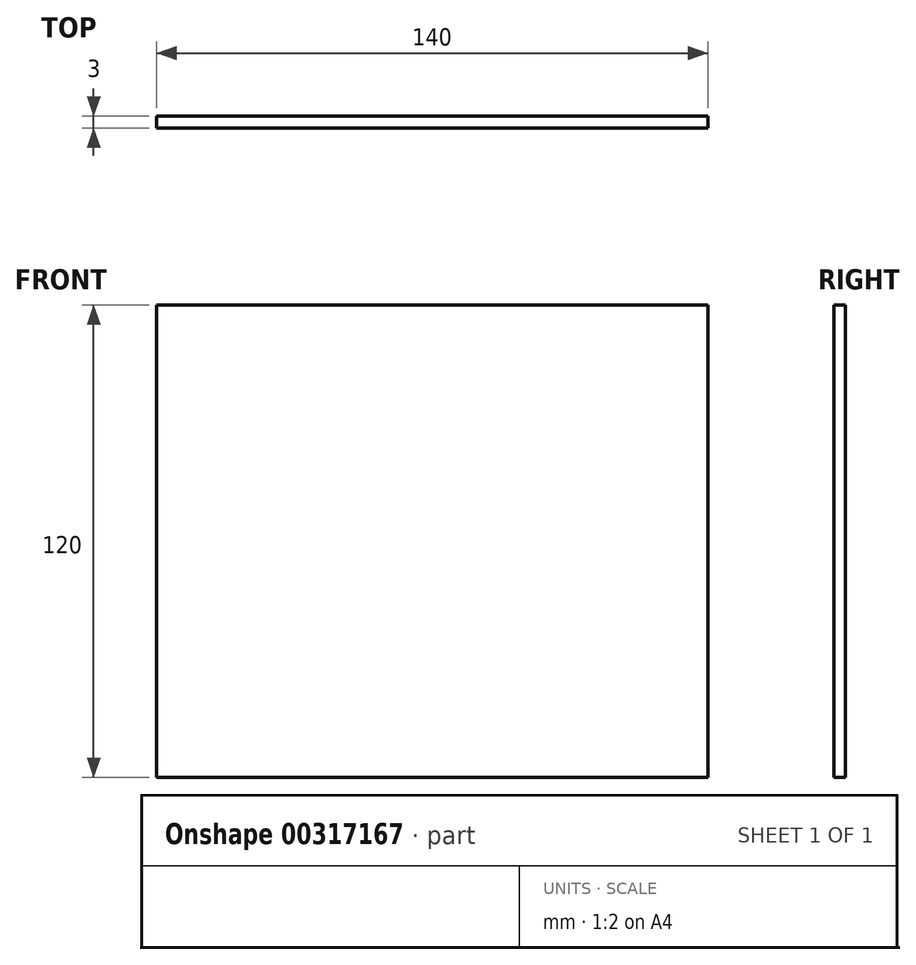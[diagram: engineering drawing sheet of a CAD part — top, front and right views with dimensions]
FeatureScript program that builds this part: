
annotation { "Feature Type Name" : "Feature", "Feature Type Description" : "" }
export const myFeature = defineFeature(function(context is Context, id is Id, definition is map)
    precondition{}
    {
        {
            var Q0;
            Q0=qCreatedBy(makeId("Front.planeOp"),FACE);
            var sketch = newSketch(context, id + "F0", { "sketchPlane" : qUnion([Q0])});
            skLineSegment(sketch, "E0.bottom", {"start": v(70, 60) * mm, "end": v(-70, 60) * mm});
            skLineSegment(sketch, "E0.top", {"start": v(70, -60) * mm, "end": v(-70, -60) * mm});
            skLineSegment(sketch, "E0.left", {"start": v(70, 60) * mm, "end": v(70, -60) * mm});
            skLineSegment(sketch, "E0.right", {"start": v(-70, 60) * mm, "end": v(-70, -60) * mm});
            skPoint(sketch, "E0.middle", {"position": v(0, 0) * mm});
            skSolve(sketch);
        }
        {
            var Q0;
            Q0=qSketchRegion(id+"F0",true);
            extrude(context, id + "F1", {"entities" : qUnion([Q0]), "depth" : 3 * mm});
        }
    });
